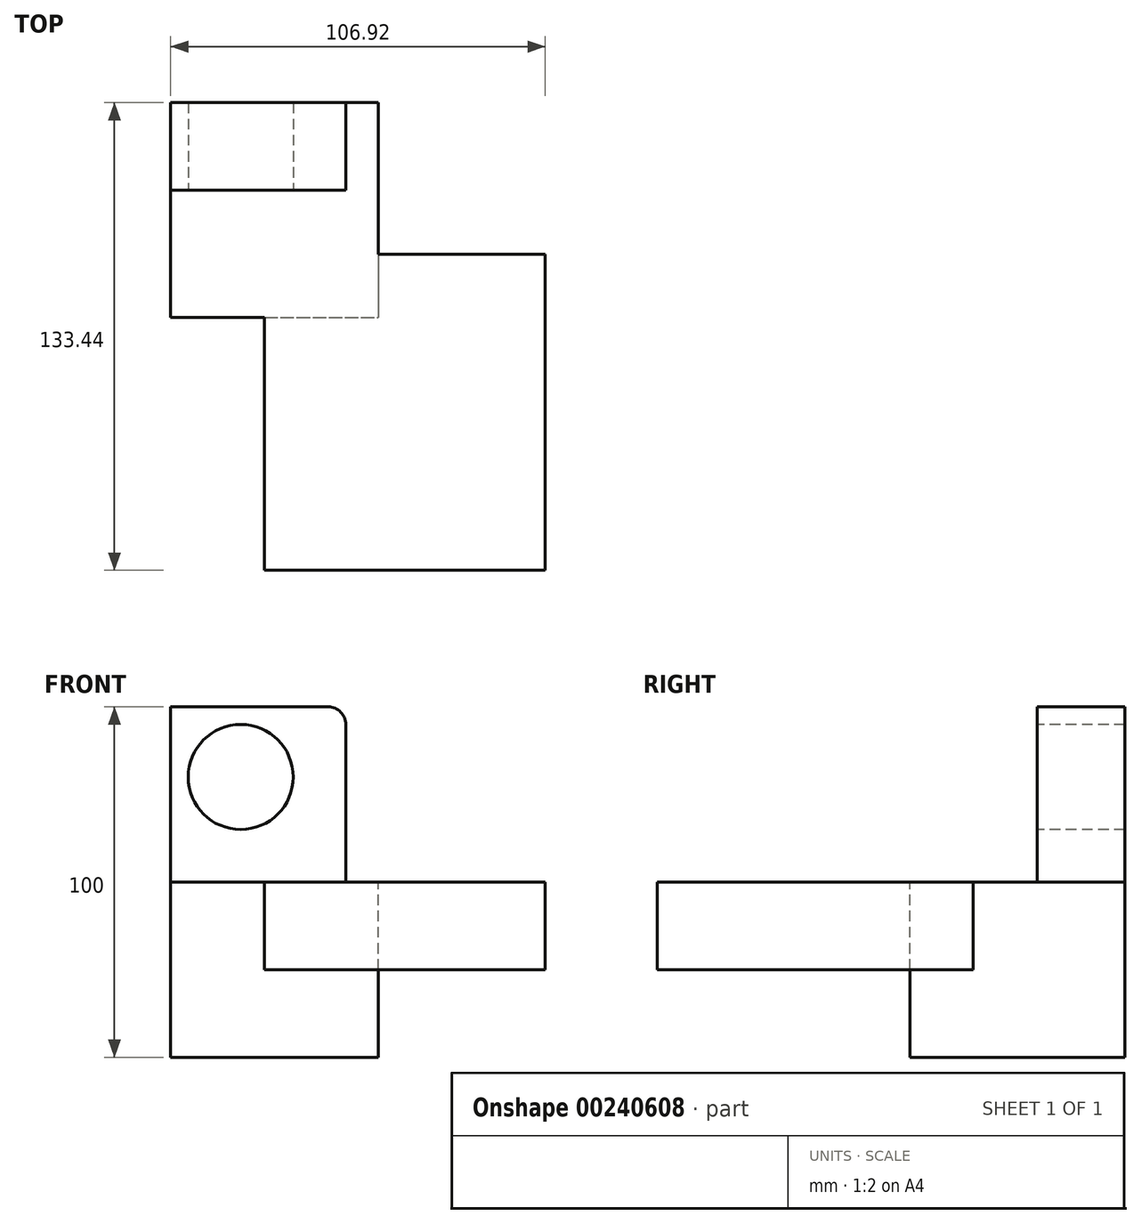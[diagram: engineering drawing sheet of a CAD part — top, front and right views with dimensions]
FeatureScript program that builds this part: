
annotation { "Feature Type Name" : "Feature", "Feature Type Description" : "" }
export const myFeature = defineFeature(function(context is Context, id is Id, definition is map)
    precondition{}
    {
        {
            var Q0;
            Q0=qCreatedBy(makeId("Front.planeOp"),FACE);
            var sketch = newSketch(context, id + "F0", { "sketchPlane" : qUnion([Q0])});
            skLineSegment(sketch, "E0.bottom", {"start": v(0, 0) * mm, "end": v(50, 0) * mm});
            skLineSegment(sketch, "E0.top", {"start": v(0, 50) * mm, "end": v(50, 50) * mm});
            skLineSegment(sketch, "E0.left", {"start": v(0, 0) * mm, "end": v(0, 50) * mm});
            skLineSegment(sketch, "E0.right", {"start": v(50, 0) * mm, "end": v(50, 50) * mm});
            skSolve(sketch);
        }
        {
            var Q0;
            Q0=makeQuery(id+"F0.imprint","IMPRINT",FACE,{"disambiguationData":[TD([[makeQuery(id+"F0.imprint","IMPRINT",EDGE,{"derivedFrom":sQuery(id+"F0.wireOp",EDGE,"E0.bottom")}),1.0]])]});
            extrude(context, id + "F1", {"entities" : qUnion([Q0]), "depth" : 25 * mm});
        }
        {
            var Q0;
            Q0=makeQuery(id+"F1.opExtrude","SWEPT_EDGE",EDGE,{"disambiguationData":[OSD([sQuery(id+"F0.wireOp",EDGE,"E0.top"),sQuery(id+"F0.wireOp",EDGE,"E0.right")])]});
            fillet(context, id + "F2", {"entities" : qUnion([Q0]), "radius" : 5 * mm, "tangentPropagation" : true, "allowEdgeOverflow" : false});
        }
        {
            var Q0;
            Q0=makeQuery(id+"F1.opExtrude","CAP_FACE",FACE,{"disambiguationData":[OSD([sQuery(id+"F0.wireOp",EDGE,"E0.bottom"),sQuery(id+"F0.wireOp",EDGE,"E0.top"),sQuery(id+"F0.wireOp",EDGE,"E0.left"),sQuery(id+"F0.wireOp",EDGE,"E0.right")])],"isStart":false});
            var sketch = newSketch(context, id + "F3", { "sketchPlane" : qUnion([Q0])});
            skCircle(sketch, "E1", {"center": v(20, 30) * mm, "radius": 15 * mm});
            skPoint(sketch, "E1.centerSnap0", {"position": v(20, 0) * mm});
            skSolve(sketch);
        }
        {
            var Q0;
            Q0=makeQuery(id+"F3.imprint","IMPRINT",FACE,{"disambiguationData":[TD([[makeQuery(id+"F3.imprint","IMPRINT",EDGE,{"derivedFrom":sQuery(id+"F3.wireOp",EDGE,"E1")}),1.0]])]});
            extrude(context, id + "F4", {"entities" : qUnion([Q0]), "operationType" : NewBodyOperationType.REMOVE, "endBound" : BoundingType.THROUGH_ALL, "oppositeDirection" : true, "depth" : 35.4 * mm});
        }
        {
            var Q0;
            Q0=qCreatedBy(makeId("Top.planeOp"),FACE);
            var sketch = newSketch(context, id + "F5", { "sketchPlane" : qUnion([Q0])});
            skLineSegment(sketch, "E2.bottom", {"start": v(0, 0) * mm, "end": v(59.28, 0) * mm});
            skLineSegment(sketch, "E2.top", {"start": v(0, -61.26) * mm, "end": v(59.28, -61.26) * mm});
            skLineSegment(sketch, "E2.left", {"start": v(0, 0) * mm, "end": v(0, -61.26) * mm});
            skLineSegment(sketch, "E2.right", {"start": v(59.28, 0) * mm, "end": v(59.28, -61.26) * mm});
            skSolve(sketch);
        }
        {
            var Q0;
            Q0 = qSketchRegion(id + "F5", true);
            extrude(context, id + "F6", {"entities" : qUnion([Q0]), "operationType" : NewBodyOperationType.ADD, "oppositeDirection" : true, "depth" : 25 * mm});
        }
        {
            var Q0;
            Q0=makeQuery(id+"F6.opExtrude","CAP_FACE",FACE,{"disambiguationData":[OSD([sQuery(id+"F5.wireOp",EDGE,"E2.bottom"),sQuery(id+"F5.wireOp",EDGE,"E2.top"),sQuery(id+"F5.wireOp",EDGE,"E2.left"),sQuery(id+"F5.wireOp",EDGE,"E2.right")])],"isStart":true});
            var sketch = newSketch(context, id + "F7", { "sketchPlane" : qUnion([Q0])});
            skLineSegment(sketch, "E3.bottom", {"start": v(38.77, -42.62) * mm, "end": v(36.2, -42.62) * mm});
            skLineSegment(sketch, "E3.top", {"start": v(38.77, -61.26) * mm, "end": v(36.2, -61.26) * mm});
            skLineSegment(sketch, "E3.left", {"start": v(38.77, -42.62) * mm, "end": v(38.77, -61.26) * mm});
            skLineSegment(sketch, "E3.right", {"start": v(36.2, -42.62) * mm, "end": v(36.2, -61.26) * mm});
            skLineSegment(sketch, "E4.bottom", {"start": v(38.77, 19.28) * mm, "end": v(38.77, 19.28) * mm});
            skLineSegment(sketch, "E4.top", {"start": v(38.77, -42.62) * mm, "end": v(38.77, -42.62) * mm});
            skLineSegment(sketch, "E4.left", {"start": v(38.77, 19.28) * mm, "end": v(38.77, -42.62) * mm});
            skLineSegment(sketch, "E4.right", {"start": v(38.77, 19.28) * mm, "end": v(38.77, -42.62) * mm});
            skLineSegment(sketch, "E5.bottom", {"start": v(38.77, 19.28) * mm, "end": v(0, 19.28) * mm});
            skLineSegment(sketch, "E5.top", {"start": v(38.77, -61.26) * mm, "end": v(0, -61.26) * mm});
            skLineSegment(sketch, "E5.left", {"start": v(38.77, 19.28) * mm, "end": v(38.77, -61.26) * mm});
            skLineSegment(sketch, "E5.right", {"start": v(0, 19.28) * mm, "end": v(0, -61.26) * mm});
            skLineSegment(sketch, "E6.bottom", {"start": v(82.93, -49.34) * mm, "end": v(75.74, -49.34) * mm});
            skLineSegment(sketch, "E6.top", {"start": v(82.93, -123.5) * mm, "end": v(75.74, -123.5) * mm});
            skLineSegment(sketch, "E6.left", {"start": v(82.93, -49.34) * mm, "end": v(82.93, -123.5) * mm});
            skLineSegment(sketch, "E6.right", {"start": v(75.74, -49.34) * mm, "end": v(75.74, -123.5) * mm});
            skLineSegment(sketch, "E7.bottom", {"start": v(106.92, -43.27) * mm, "end": v(26.76, -43.27) * mm});
            skLineSegment(sketch, "E7.top", {"start": v(106.92, -133.44) * mm, "end": v(26.76, -133.44) * mm});
            skLineSegment(sketch, "E7.left", {"start": v(106.92, -43.27) * mm, "end": v(106.92, -133.44) * mm});
            skLineSegment(sketch, "E7.right", {"start": v(26.76, -43.27) * mm, "end": v(26.76, -133.44) * mm});
            skSolve(sketch);
        }
        {
            var Q0;
            Q0=makeQuery(id+"F6.opExtrude","CAP_FACE",FACE,{"disambiguationData":[OSD([sQuery(id+"F5.wireOp",EDGE,"E2.bottom"),sQuery(id+"F5.wireOp",EDGE,"E2.top"),sQuery(id+"F5.wireOp",EDGE,"E2.left"),sQuery(id+"F5.wireOp",EDGE,"E2.right")])],"isStart":false});
            var Q1;
            Q1=makeQuery(id+"F7.imprint","IMPRINT",FACE,{"disambiguationData":[TD([[makeQuery(id+"F7.imprint","IMPRINT",EDGE,{"derivedFrom":sQuery(id+"F7.wireOp",EDGE,"E6.bottom")}),1.0]])]});
            var Q2;
            Q2=makeQuery(id+"F7.imprint","IMPRINT",FACE,{"disambiguationData":[TD([[makeQuery(id+"F7.imprint","IMPRINT",EDGE,{"derivedFrom":sQuery(id+"F7.wireOp",EDGE,"E6.bottom")}),-1.0]])]});
            extrude(context, id + "F8", {"entities" : qUnion([Q0, Q1, Q2]), "operationType" : NewBodyOperationType.ADD, "depth" : 25 * mm});
        }
    });
